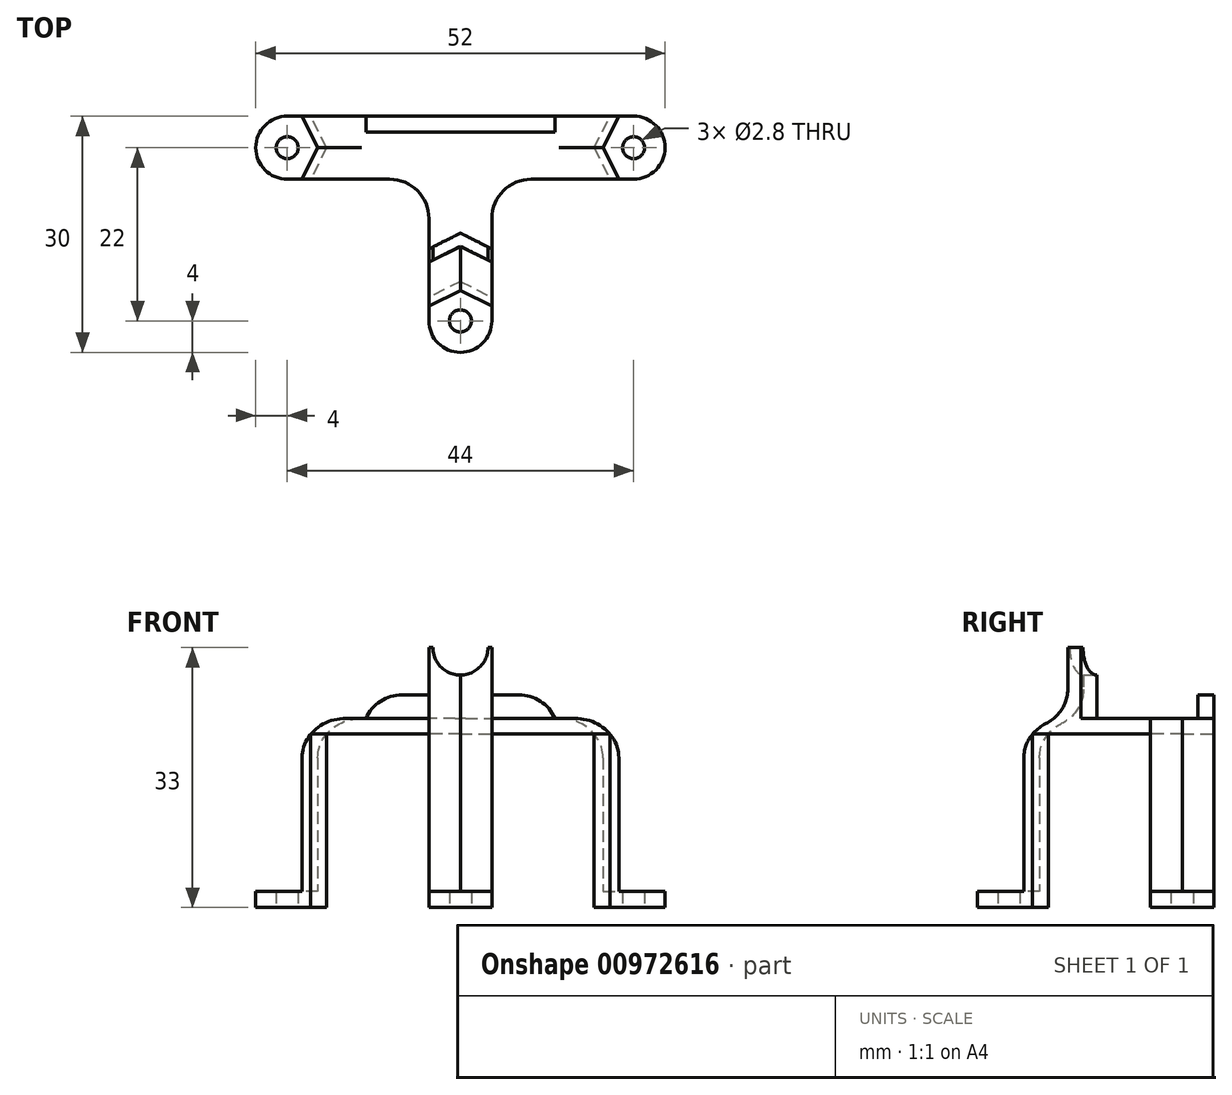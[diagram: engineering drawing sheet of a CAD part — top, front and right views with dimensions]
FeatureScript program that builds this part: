
annotation { "Feature Type Name" : "Feature", "Feature Type Description" : "" }
export const myFeature = defineFeature(function(context is Context, id is Id, definition is map)
    precondition{}
    {
        {
            var Q0;
            Q0=qCreatedBy(makeId("Top.planeOp"),FACE);
            var sketch = newSketch(context, id + "F0", { "sketchPlane" : qUnion([Q0])});
            skLineSegment(sketch, "E0", {"start": v(0, 0) * mm, "end": v(22, 0) * mm, "construction": true});
            skCircle(sketch, "E1", {"center": v(22, 0) * mm, "radius": 1.4 * mm});
            skLineSegment(sketch, "E2", {"start": v(0, 0) * mm, "end": v(0, -22) * mm, "construction": true});
            skCircle(sketch, "E3", {"center": v(0, -22) * mm, "radius": 1.4 * mm});
            skCircle(sketch, "E4", {"center": v(22, 0) * mm, "radius": 4 * mm});
            skCircle(sketch, "E5", {"center": v(0, -22) * mm, "radius": 4 * mm});
            skPoint(sketch, "E6", {"position": v(17, 0) * mm});
            skLineSegment(sketch, "E7", {"start": v(17, 0) * mm, "end": v(19, 4) * mm});
            skLineSegment(sketch, "E8", {"start": v(19, 4) * mm, "end": v(22, 4) * mm});
            skLineSegment(sketch, "E9.MirrorCS", {"start": v(19, -4) * mm, "end": v(22, -4) * mm});
            skLineSegment(sketch, "E10.MirrorCS", {"start": v(17, 0) * mm, "end": v(19, -4) * mm});
            skPoint(sketch, "E11", {"position": v(0, -17) * mm});
            skLineSegment(sketch, "E12", {"start": v(4, -19) * mm, "end": v(4, -22) * mm});
            skLineSegment(sketch, "E13", {"start": v(0, -17) * mm, "end": v(4, -19) * mm});
            skLineSegment(sketch, "E14.MirrorCS", {"start": v(0, -17) * mm, "end": v(-4, -19) * mm});
            skLineSegment(sketch, "E15.MirrorCS", {"start": v(-4, -19) * mm, "end": v(-4, -22) * mm});
            skSolve(sketch);
        }
        {
            var Q0;
            Q0 = qSketchRegion(id + "F0", true);
            extrude(context, id + "F1", {"entities" : qUnion([Q0]), "depth" : 2 * mm, "offsetDistance" : 25 * mm});
        }
        {
            var Q0;
            Q0=makeQuery(id+"F1.opExtrude","CAP_FACE",FACE,{"disambiguationData":[OSD([sQuery(id+"F0.wireOp",EDGE,"E1"),sQuery(id+"F0.wireOp",EDGE,"E4"),sQuery(id+"F0.wireOp",EDGE,"E7"),sQuery(id+"F0.wireOp",EDGE,"E8"),sQuery(id+"F0.wireOp",EDGE,"E9.MirrorCS"),sQuery(id+"F0.wireOp",EDGE,"E10.MirrorCS")])],"isStart":false});
            var sketch = newSketch(context, id + "F2", { "sketchPlane" : qUnion([Q0])});
            skLineSegment(sketch, "E16.0", {"start": v(17, 0) * mm, "end": v(19, 4) * mm});
            skPoint(sketch, "E17.0", {"position": v(18, -2) * mm});
            skLineSegment(sketch, "E18.0", {"start": v(17, 0) * mm, "end": v(19, -4) * mm});
            skPoint(sketch, "E19.0", {"position": v(2, -18) * mm});
            skLineSegment(sketch, "E20.0", {"start": v(0, -17) * mm, "end": v(4, -19) * mm});
            skLineSegment(sketch, "E21.0", {"start": v(0, -17) * mm, "end": v(-4, -19) * mm});
            skLineSegment(sketch, "E22.0", {"start": v(18.12, 0) * mm, "end": v(20.12, 4) * mm});
            skLineSegment(sketch, "E22.1", {"start": v(18.12, 0) * mm, "end": v(20.12, -4) * mm});
            skLineSegment(sketch, "E23", {"start": v(19, 4) * mm, "end": v(20.12, 4) * mm});
            skLineSegment(sketch, "E24", {"start": v(19, -4) * mm, "end": v(20.12, -4) * mm});
            skLineSegment(sketch, "E25.0", {"start": v(0, -18.12) * mm, "end": v(4, -20.12) * mm});
            skLineSegment(sketch, "E25.1", {"start": v(0, -18.12) * mm, "end": v(-4, -20.12) * mm});
            skLineSegment(sketch, "E26", {"start": v(4, -19) * mm, "end": v(4, -20.12) * mm});
            skLineSegment(sketch, "E27", {"start": v(-4, -19) * mm, "end": v(-4, -20.12) * mm});
            skSolve(sketch);
        }
        {
            var Q0;
            Q0 = qSketchRegion(id + "F2", true);
            extrude(context, id + "F3", {"entities" : qUnion([Q0]), "operationType" : NewBodyOperationType.ADD, "depth" : 20 * mm, "offsetDistance" : 25 * mm});
        }
        {
            var Q0;
            Q0=makeQuery(id+"F3.opExtrude","CAP_FACE",FACE,{"disambiguationData":[OSD([sQuery(id+"F2.wireOp",EDGE,"E16.0"),sQuery(id+"F2.wireOp",EDGE,"E18.0"),sQuery(id+"F2.wireOp",EDGE,"E22.0"),sQuery(id+"F2.wireOp",EDGE,"E22.1"),sQuery(id+"F2.wireOp",EDGE,"E23"),sQuery(id+"F2.wireOp",EDGE,"E24")])],"isStart":false});
            var sketch = newSketch(context, id + "F4", { "sketchPlane" : qUnion([Q0])});
            skLineSegment(sketch, "E28", {"start": v(20.12, 4) * mm, "end": v(0, 4) * mm});
            skLineSegment(sketch, "E29", {"start": v(20.12, -4) * mm, "end": v(0, -4) * mm});
            skPoint(sketch, "E30.0", {"position": v(4, -20.12) * mm});
            skPoint(sketch, "E31.0", {"position": v(0, -18.12) * mm});
            skLineSegment(sketch, "E32", {"start": v(4, -20.12) * mm, "end": v(4, -4) * mm});
            skLineSegment(sketch, "E33", {"start": v(0, -18.12) * mm, "end": v(0, 4) * mm});
            skLineSegment(sketch, "E34.0", {"start": v(0, -18.12) * mm, "end": v(4, -20.12) * mm});
            skSolve(sketch);
        }
        {
            var Q0;
            Q0 = qSketchRegion(id + "F4", true);
            var Q1;
            {var subQ7=makeQuery(id+"F3.opExtrude","CAP_EDGE",EDGE,{"disambiguationData":[OSD([sQuery(id+"F2.wireOp",EDGE,"E16.0")])],"isStart":false});Q1=makeQuery(id+"F4.imprint","IMPRINT",FACE,{"disambiguationData":[TD([[makeQuery(id+"F4.imprint","IMPRINT",EDGE,{"derivedFrom":subQ7}),1.0]])]});}
            var Q2;
            {var subQ1=makeQuery(id+"F3.opExtrude","CAP_EDGE",EDGE,{"disambiguationData":[OSD([sQuery(id+"F2.wireOp",EDGE,"E16.0")])],"isStart":false});Q2=makeQuery(id+"F4.imprint","IMPRINT",FACE,{"disambiguationData":[TD([[makeQuery(id+"F4.imprint","IMPRINT",EDGE,{"derivedFrom":subQ1}),-1.0]])]});}
            extrude(context, id + "F5", {"entities" : qUnion([Q0, Q1, Q2]), "operationType" : NewBodyOperationType.ADD, "depth" : 2 * mm, "offsetDistance" : 25 * mm});
        }
        {
            var Q0;
            Q0=makeQuery(id+"F5.opExtrude","CAP_FACE",FACE,{"disambiguationData":[OSD([sQuery(id+"F2.wireOp",EDGE,"E22.0"),sQuery(id+"F2.wireOp",EDGE,"E22.1"),sQuery(id+"F4.wireOp",EDGE,"E28"),sQuery(id+"F4.wireOp",EDGE,"E29"),sQuery(id+"F4.wireOp",EDGE,"E32"),sQuery(id+"F4.wireOp",EDGE,"E33"),sQuery(id+"F4.wireOp",EDGE,"E34.0")])],"isStart":false});
            var sketch = newSketch(context, id + "F6", { "sketchPlane" : qUnion([Q0])});
            skLineSegment(sketch, "E35.bottom", {"start": v(0, 21.64) * mm, "end": v(-24.26, 21.64) * mm});
            skLineSegment(sketch, "E35.top", {"start": v(0, -43.46) * mm, "end": v(-24.26, -43.46) * mm});
            skLineSegment(sketch, "E35.left", {"start": v(0, 21.64) * mm, "end": v(0, -43.46) * mm});
            skLineSegment(sketch, "E35.right", {"start": v(-24.26, 21.64) * mm, "end": v(-24.26, -43.46) * mm});
            skSolve(sketch);
        }
        {
            var Q0;
            Q0 = qSketchRegion(id + "F6", true);
            extrude(context, id + "F7", {"entities" : qUnion([Q0]), "operationType" : NewBodyOperationType.REMOVE, "oppositeDirection" : true, "depth" : 25 * mm, "offsetDistance" : 25 * mm});
        }
        {
            var Q0;
            Q0=makeQuery(id+"F5.opExtrude","SWEPT_EDGE",EDGE,{"disambiguationData":[OSD([sQuery(id+"F4.wireOp",EDGE,"E29"),sQuery(id+"F4.wireOp",EDGE,"E32")])]});
            var Q1;
            Q1=makeQuery(id+"F3.opExtrude","CAP_EDGE",EDGE,{"disambiguationData":[OSD([sQuery(id+"F2.wireOp",EDGE,"E20.0")])],"isStart":false});
            var Q2;
            Q2=makeQuery(id+"F3.opExtrude","CAP_EDGE",EDGE,{"disambiguationData":[OSD([sQuery(id+"F2.wireOp",EDGE,"E18.0")])],"isStart":false});
            var Q3;
            Q3=makeQuery(id+"F3.opExtrude","CAP_EDGE",EDGE,{"disambiguationData":[OSD([sQuery(id+"F2.wireOp",EDGE,"E16.0")])],"isStart":false});
            var Q4;
            Q4=makeQuery(id+"F5.opExtrude","CAP_EDGE",EDGE,{"disambiguationData":[OSD([sQuery(id+"F2.wireOp",EDGE,"E22.1")])],"isStart":false});
            var Q5;
            Q5=makeQuery(id+"F5.opExtrude","CAP_EDGE",EDGE,{"disambiguationData":[OSD([sQuery(id+"F2.wireOp",EDGE,"E22.0")])],"isStart":false});
            var Q6;
            Q6=makeQuery(id+"F5.opExtrude","CAP_EDGE",EDGE,{"disambiguationData":[OSD([sQuery(id+"F4.wireOp",EDGE,"E34.0")])],"isStart":false});
            fillet(context, id + "F8", {"entities" : qUnion([Q0, Q1, Q2, Q3, Q4, Q5, Q6]), "radius" : 5 * mm, "tangentPropagation" : true, "allowEdgeOverflow" : false});
        }
        {
            var Q0;
            Q0=makeQuery(id+"F5.opExtrude","CAP_FACE",FACE,{"disambiguationData":[OSD([sQuery(id+"F2.wireOp",EDGE,"E22.0"),sQuery(id+"F2.wireOp",EDGE,"E22.1"),sQuery(id+"F4.wireOp",EDGE,"E28"),sQuery(id+"F4.wireOp",EDGE,"E29"),sQuery(id+"F4.wireOp",EDGE,"E32"),sQuery(id+"F4.wireOp",EDGE,"E33"),sQuery(id+"F4.wireOp",EDGE,"E34.0")])],"isStart":false});
            var sketch = newSketch(context, id + "F9", { "sketchPlane" : qUnion([Q0])});
            skLineSegment(sketch, "E36.0", {"start": v(0, -12.53) * mm, "end": v(4, -14.53) * mm});
            skLineSegment(sketch, "E37.0", {"start": v(0.67, -11.19) * mm, "end": v(4, -12.85) * mm});
            skLineSegment(sketch, "E38", {"start": v(0.67, -11.19) * mm, "end": v(0, -10.85) * mm});
            skLineSegment(sketch, "E39", {"start": v(0, -12.53) * mm, "end": v(0, -10.85) * mm});
            skLineSegment(sketch, "E40", {"start": v(4, -14.53) * mm, "end": v(4, -12.85) * mm});
            skSolve(sketch);
        }
        {
            var Q0;
            Q0 = qSketchRegion(id + "F9", true);
            extrude(context, id + "F10", {"entities" : qUnion([Q0]), "operationType" : NewBodyOperationType.ADD, "depth" : 9 * mm, "offsetDistance" : 25 * mm});
        }
        {
            var Q0;
            Q0=makeQuery(id+"F10.opExtrude","CAP_EDGE",EDGE,{"disambiguationData":[OSD([sQuery(id+"F9.wireOp",EDGE,"E37.0"),sQuery(id+"F9.wireOp",EDGE,"E38")])],"isStart":true});
            var Q1;
            {var subQ0=sQuery(id+"F4.wireOp",EDGE,"E34.0");Q1=makeQuery(id+"F10.boolean.opBoolean","MERGE",EDGE,{"derivedFrom":[makeQuery(id+"F8.opFillet","BLEND_EDGE",EDGE,{"blendedFrom":[makeQuery(id+"F5.opExtrude","CAP_EDGE",EDGE,{"disambiguationData":[OSD([subQ0])],"isStart":false}),makeQuery(id+"F5.opExtrude","CAP_FACE",FACE,{"disambiguationData":[OSD([sQuery(id+"F2.wireOp",EDGE,"E22.0"),sQuery(id+"F2.wireOp",EDGE,"E22.1"),sQuery(id+"F4.wireOp",EDGE,"E28"),sQuery(id+"F4.wireOp",EDGE,"E29"),sQuery(id+"F4.wireOp",EDGE,"E32"),sQuery(id+"F4.wireOp",EDGE,"E33"),subQ0])],"isStart":false})],"blendedInto":[makeQuery(id+"F5.opExtrude","CAP_FACE",FACE,{"disambiguationData":[OSD([sQuery(id+"F2.wireOp",EDGE,"E22.0"),sQuery(id+"F2.wireOp",EDGE,"E22.1"),sQuery(id+"F4.wireOp",EDGE,"E28"),sQuery(id+"F4.wireOp",EDGE,"E29"),sQuery(id+"F4.wireOp",EDGE,"E32"),sQuery(id+"F4.wireOp",EDGE,"E33"),subQ0])],"isStart":false})]}),makeQuery(id+"F10.opExtrude","CAP_EDGE",EDGE,{"disambiguationData":[OSD([sQuery(id+"F9.wireOp",EDGE,"E36.0")])],"isStart":true})]});}
            fillet(context, id + "F11", {"entities" : qUnion([Q0, Q1]), "radius" : 5 * mm, "tangentPropagation" : true, "allowEdgeOverflow" : false});
        }
        {
            var Q0;
            Q0=makeQuery(id+"F5.opExtrude","CAP_FACE",FACE,{"disambiguationData":[OSD([sQuery(id+"F2.wireOp",EDGE,"E22.0"),sQuery(id+"F2.wireOp",EDGE,"E22.1"),sQuery(id+"F4.wireOp",EDGE,"E28"),sQuery(id+"F4.wireOp",EDGE,"E29"),sQuery(id+"F4.wireOp",EDGE,"E32"),sQuery(id+"F4.wireOp",EDGE,"E33"),sQuery(id+"F4.wireOp",EDGE,"E34.0")])],"isStart":false});
            var sketch = newSketch(context, id + "F12", { "sketchPlane" : qUnion([Q0])});
            skPoint(sketch, "E41", {"position": v(12, 4) * mm});
            skPoint(sketch, "E42.orphan", {"position": v(14.53, 4) * mm});
            skPoint(sketch, "E43.0.start.orphan", {"position": v(12.53, 0) * mm});
            skLineSegment(sketch, "E44.0", {"start": v(12.2, 4) * mm, "end": v(0, 4) * mm});
            skLineSegment(sketch, "E45.0", {"start": v(12.2, 2) * mm, "end": v(0, 2) * mm});
            skLineSegment(sketch, "E46", {"start": v(0, 4) * mm, "end": v(0, 2) * mm});
            skLineSegment(sketch, "E47", {"start": v(12, 4) * mm, "end": v(12, 2) * mm});
            skSolve(sketch);
        }
        {
            var Q0;
            Q0 = qSketchRegion(id + "F12", true);
            extrude(context, id + "F13", {"entities" : qUnion([Q0]), "operationType" : NewBodyOperationType.ADD, "depth" : 3 * mm, "offsetDistance" : 25 * mm});
        }
        {
            var Q0;
            Q0=makeQuery(id+"F13.opExtrude","CAP_EDGE",EDGE,{"disambiguationData":[OSD([sQuery(id+"F12.wireOp",EDGE,"E47")])],"isStart":false});
            fillet(context, id + "F14", {"entities" : qUnion([Q0]), "radius" : 5 * mm, "tangentPropagation" : true, "allowEdgeOverflow" : false});
        }
        {
            var Q0;
            Q0=makeQuery(id+"F1.opExtrude","SWEPT_BODY",BODY,{"disambiguationData":[OSD([sQuery(id+"F0.wireOp",EDGE,"E1"),sQuery(id+"F0.wireOp",EDGE,"E4"),sQuery(id+"F0.wireOp",EDGE,"E7"),sQuery(id+"F0.wireOp",EDGE,"E8"),sQuery(id+"F0.wireOp",EDGE,"E9.MirrorCS"),sQuery(id+"F0.wireOp",EDGE,"E10.MirrorCS")])]});
            var Q1;
            Q1=makeQuery(id+"F13.boolean.opBoolean","MERGE",FACE,{"derivedFrom":[makeQuery(id+"F10.boolean.opBoolean","MERGE",FACE,{"derivedFrom":[makeQuery(id+"F7.boolean.opBoolean","MERGE",FACE,{"derivedFrom":[makeQuery(id+"F5.opExtrude","SWEPT_FACE",FACE,{"disambiguationData":[OSD([sQuery(id+"F4.wireOp",EDGE,"E33")])]})],"fromTools":[makeQuery(id+"F7.opExtrude","SWEPT_FACE",FACE,{"disambiguationData":[OSD([sQuery(id+"F6.wireOp",EDGE,"E35.left")])]})]}),makeQuery(id+"F10.opExtrude","SWEPT_FACE",FACE,{"disambiguationData":[OSD([sQuery(id+"F9.wireOp",EDGE,"E39")])]})]}),makeQuery(id+"F13.opExtrude","SWEPT_FACE",FACE,{"disambiguationData":[OSD([sQuery(id+"F12.wireOp",EDGE,"E46")])]})]});
            mirror(context, id + "F15", {"operationType" : NewBodyOperationType.ADD, "entities" : qUnion([Q0]), "mirrorPlane" : qUnion([Q1])});
        }
        {
            var Q0;
            {var subQ0=makeQuery(id+"F13.boolean.opBoolean","MERGE",FACE,{"derivedFrom":[makeQuery(id+"F5.boolean.opBoolean","MERGE",FACE,{"derivedFrom":[makeQuery(id+"F3.boolean.opBoolean","MERGE",FACE,{"derivedFrom":[makeQuery(id+"F1.opExtrude","SWEPT_FACE",FACE,{"disambiguationData":[OSD([sQuery(id+"F0.wireOp",EDGE,"E8")])]}),makeQuery(id+"F3.opExtrude","SWEPT_FACE",FACE,{"disambiguationData":[OSD([sQuery(id+"F2.wireOp",EDGE,"E23")])]})]}),makeQuery(id+"F5.opExtrude","SWEPT_FACE",FACE,{"disambiguationData":[OSD([sQuery(id+"F4.wireOp",EDGE,"E28")])]})]}),makeQuery(id+"F13.opExtrude","SWEPT_FACE",FACE,{"disambiguationData":[OSD([sQuery(id+"F12.wireOp",EDGE,"E44.0")])]})]});Q0=makeQuery(id+"F15.boolean.opBoolean","MERGE",FACE,{"derivedFrom":[subQ0,makeQuery(id+"F15.opPattern","COPY",FACE,{"derivedFrom":subQ0,"instanceName":"1"})]});}
            var sketch = newSketch(context, id + "F16", { "sketchPlane" : qUnion([Q0])});
            skPoint(sketch, "E48", {"position": v(0, 33) * mm});
            skCircle(sketch, "E49", {"center": v(0, 33) * mm, "radius": 3.5 * mm});
            skSolve(sketch);
        }
        {
            var Q0;
            Q0 = qSketchRegion(id + "F16", true);
            extrude(context, id + "F17", {"entities" : qUnion([Q0]), "operationType" : NewBodyOperationType.REMOVE, "oppositeDirection" : true, "depth" : 25 * mm, "offsetDistance" : 25 * mm});
        }
    });
